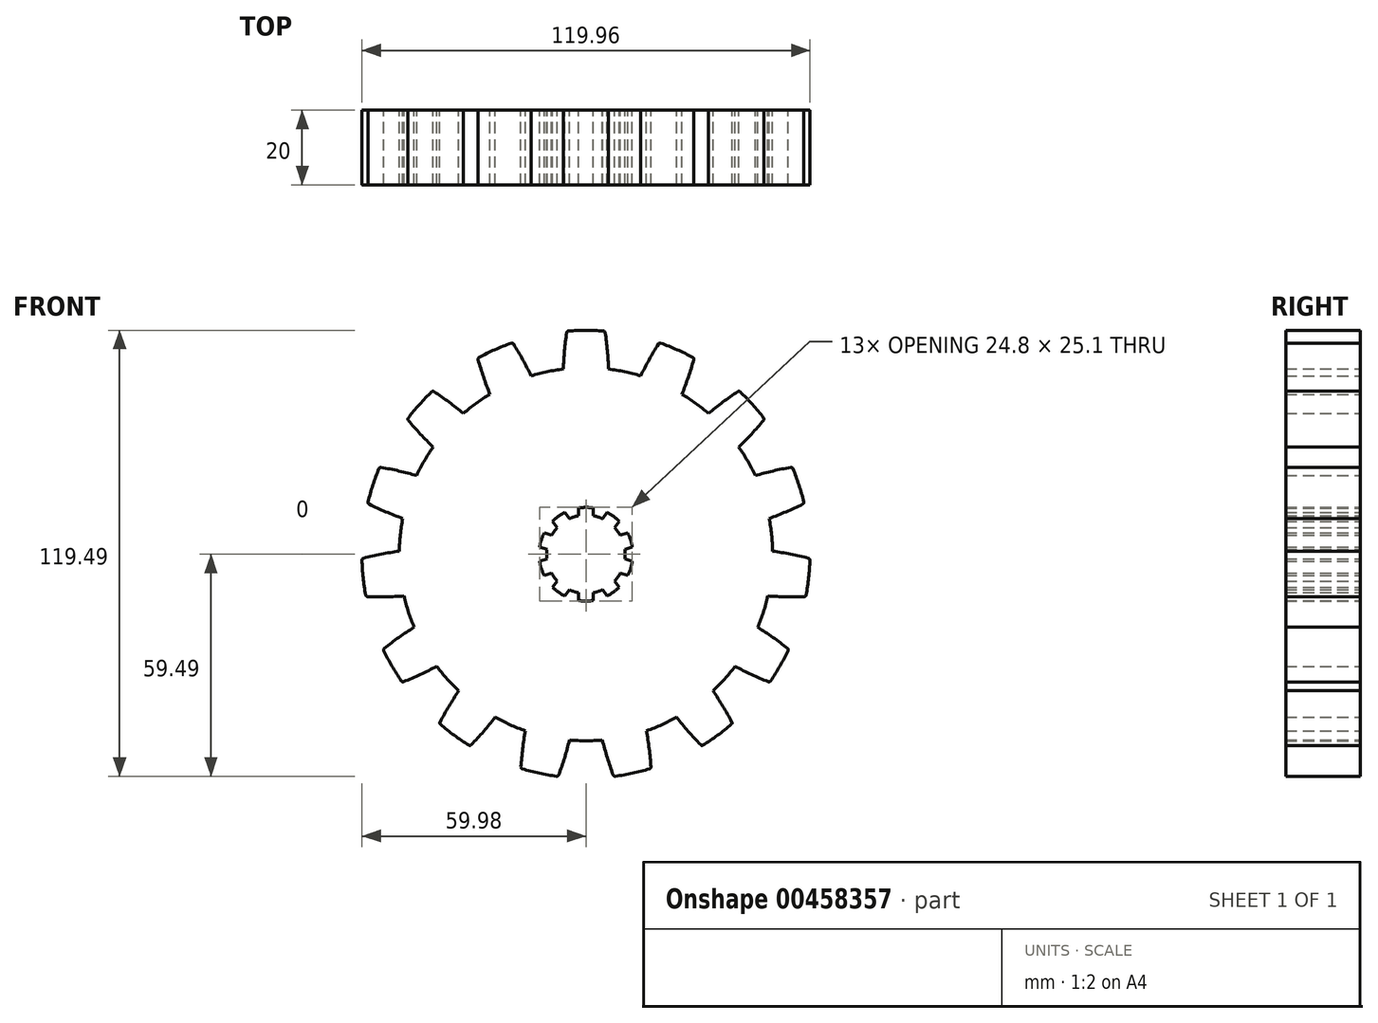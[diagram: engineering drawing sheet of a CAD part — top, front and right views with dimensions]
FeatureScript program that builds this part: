
annotation { "Feature Type Name" : "Feature", "Feature Type Description" : "" }
export const myFeature = defineFeature(function(context is Context, id is Id, definition is map)
    precondition{}
    {
        {
            var Q0;
            Q0=qCreatedBy(makeId("Front.planeOp"),FACE);
            var sketch = newSketch(context, id + "F0", { "sketchPlane" : qUnion([Q0])});
            skCircle(sketch, "E0", {"center": v(0, 0) * mm, "radius": 50 * mm});
            skArc(sketch, "E1", {"start": v(-5.11, 59.78) * mm, "mid": v(-5.72, 54.72) * mm, "end": v(-6.05, 49.63) * mm});
            skArc(sketch, "E2.trimOffspring", {"start": v(5.11, 59.78) * mm, "mid": v(0, 60) * mm, "end": v(-5.11, 59.78) * mm});
            skArc(sketch, "E3.trimOffspring", {"start": v(6.05, 49.63) * mm, "mid": v(5.72, 54.72) * mm, "end": v(5.11, 59.78) * mm});
            skPoint(sketch, "E4.start.orphan", {"position": v(0, 46.5) * mm});
            skArc(sketch, "E5.1.0", {"start": v(-19.64, 56.7) * mm, "mid": v(-24.4, 54.81) * mm, "end": v(-28.99, 52.53) * mm});
            skArc(sketch, "E5.1.1", {"start": v(-14.66, 47.8) * mm, "mid": v(-17.03, 52.32) * mm, "end": v(-19.64, 56.7) * mm});
            skArc(sketch, "E5.1.2", {"start": v(-28.99, 52.53) * mm, "mid": v(-27.49, 47.66) * mm, "end": v(-25.71, 42.88) * mm});
            skArc(sketch, "E5.2.0", {"start": v(-41, 43.8) * mm, "mid": v(-44.59, 40.15) * mm, "end": v(-47.85, 36.2) * mm});
            skArc(sketch, "E5.2.1", {"start": v(-32.84, 37.7) * mm, "mid": v(-36.84, 40.87) * mm, "end": v(-41, 43.8) * mm});
            skArc(sketch, "E5.2.2", {"start": v(-47.85, 36.2) * mm, "mid": v(-44.5, 32.36) * mm, "end": v(-40.93, 28.72) * mm});
            skArc(sketch, "E6.3.3.0", {"start": v(-55.28, 23.34) * mm, "mid": v(-57.06, 18.54) * mm, "end": v(-58.44, 13.6) * mm});
            skArc(sketch, "E6.4.3.0", {"start": v(-45.34, 21.09) * mm, "mid": v(-50.27, 22.35) * mm, "end": v(-55.28, 23.34) * mm});
            skArc(sketch, "E6.8.3.0", {"start": v(-58.44, 13.6) * mm, "mid": v(-53.81, 11.47) * mm, "end": v(-49.07, 9.59) * mm});
            skArc(sketch, "E6.3.4.0", {"start": v(-59.99, -1.16) * mm, "mid": v(-59.67, -6.27) * mm, "end": v(-58.92, -11.34) * mm});
            skArc(sketch, "E6.4.4.0", {"start": v(-50, 0.82) * mm, "mid": v(-55.02, -0.03) * mm, "end": v(-59.99, -1.16) * mm});
            skArc(sketch, "E6.8.4.0", {"start": v(-58.92, -11.34) * mm, "mid": v(-53.82, -11.41) * mm, "end": v(-48.73, -11.2) * mm});
            skArc(sketch, "E6.3.5.0", {"start": v(-54.33, -25.46) * mm, "mid": v(-51.96, -30) * mm, "end": v(-49.22, -34.32) * mm});
            skArc(sketch, "E6.4.5.0", {"start": v(-46, -19.58) * mm, "mid": v(-50.25, -22.4) * mm, "end": v(-54.33, -25.46) * mm});
            skArc(sketch, "E6.8.5.0", {"start": v(-49.22, -34.32) * mm, "mid": v(-44.53, -32.32) * mm, "end": v(-39.96, -30.05) * mm});
            skArc(sketch, "E6.3.6.0", {"start": v(-39.28, -45.36) * mm, "mid": v(-35.27, -48.54) * mm, "end": v(-31, -51.37) * mm});
            skArc(sketch, "E6.4.6.0", {"start": v(-34.06, -36.6) * mm, "mid": v(-36.8, -40.9) * mm, "end": v(-39.28, -45.36) * mm});
            skArc(sketch, "E6.8.6.0", {"start": v(-31, -51.37) * mm, "mid": v(-27.53, -47.63) * mm, "end": v(-24.28, -43.7) * mm});
            skArc(sketch, "E6.3.7.0", {"start": v(-17.43, -57.41) * mm, "mid": v(-12.47, -58.69) * mm, "end": v(-7.43, -59.54) * mm});
            skArc(sketch, "E6.4.7.0", {"start": v(-16.23, -47.3) * mm, "mid": v(-16.98, -52.33) * mm, "end": v(-17.43, -57.41) * mm});
            skArc(sketch, "E6.8.7.0", {"start": v(-7.43, -59.54) * mm, "mid": v(-5.78, -54.71) * mm, "end": v(-4.4, -49.8) * mm});
            skArc(sketch, "E6.3.8.0", {"start": v(7.43, -59.54) * mm, "mid": v(12.47, -58.69) * mm, "end": v(17.43, -57.41) * mm});
            skArc(sketch, "E6.4.8.0", {"start": v(4.4, -49.8) * mm, "mid": v(5.78, -54.71) * mm, "end": v(7.43, -59.54) * mm});
            skArc(sketch, "E6.8.8.0", {"start": v(17.43, -57.41) * mm, "mid": v(16.98, -52.33) * mm, "end": v(16.23, -47.3) * mm});
            skArc(sketch, "E6.3.9.0", {"start": v(31, -51.37) * mm, "mid": v(35.27, -48.54) * mm, "end": v(39.28, -45.36) * mm});
            skArc(sketch, "E6.4.9.0", {"start": v(24.28, -43.7) * mm, "mid": v(27.53, -47.63) * mm, "end": v(31, -51.37) * mm});
            skArc(sketch, "E6.8.9.0", {"start": v(39.28, -45.36) * mm, "mid": v(36.8, -40.9) * mm, "end": v(34.06, -36.6) * mm});
            skArc(sketch, "E7", {"start": v(-7.68, 7.16) * mm, "mid": v(-8.5, 6.17) * mm, "end": v(-9.19, 5.09) * mm});
            skArc(sketch, "E8", {"start": v(2, 12.39) * mm, "mid": v(0, 12.55) * mm, "end": v(-2, 12.39) * mm});
            skLineSegment(sketch, "E9.left", {"start": v(2, 12.39) * mm, "end": v(2, 10.3) * mm});
            skLineSegment(sketch, "E9.right", {"start": v(-2, 12.39) * mm, "end": v(-2, 10.3) * mm});
            skPoint(sketch, "E10.orphan", {"position": v(-2, 13) * mm});
            skPoint(sketch, "E11.orphan", {"position": v(2, 13) * mm});
            skPoint(sketch, "E12.trimOffspring.end.orphan", {"position": v(2, -13) * mm});
            skPoint(sketch, "E13.trimOffspring.end.orphan", {"position": v(-2, -13) * mm});
            skArc(sketch, "E14.1.0", {"start": v(-5.66, 11.2) * mm, "mid": v(-7.38, 10.15) * mm, "end": v(-8.9, 8.85) * mm});
            skLineSegment(sketch, "E14.1.1", {"start": v(-8.9, 8.85) * mm, "end": v(-7.68, 7.16) * mm});
            skLineSegment(sketch, "E14.1.2", {"start": v(-5.66, 11.2) * mm, "end": v(-4.44, 9.51) * mm});
            skArc(sketch, "E14.2.0", {"start": v(-11.17, 5.73) * mm, "mid": v(-11.94, 3.88) * mm, "end": v(-12.4, 1.93) * mm});
            skLineSegment(sketch, "E14.2.1", {"start": v(-12.4, 1.93) * mm, "end": v(-10.42, 1.28) * mm});
            skLineSegment(sketch, "E14.2.2", {"start": v(-11.17, 5.73) * mm, "end": v(-9.19, 5.09) * mm});
            skArc(sketch, "E15.3.3.0", {"start": v(-12.4, -1.93) * mm, "mid": v(-11.94, -3.88) * mm, "end": v(-11.17, -5.73) * mm});
            skLineSegment(sketch, "E15.4.3.0", {"start": v(-11.17, -5.73) * mm, "end": v(-9.19, -5.09) * mm});
            skLineSegment(sketch, "E15.7.3.0", {"start": v(-12.4, -1.93) * mm, "end": v(-10.42, -1.28) * mm});
            skArc(sketch, "E15.3.4.0", {"start": v(-8.9, -8.85) * mm, "mid": v(-7.38, -10.15) * mm, "end": v(-5.66, -11.2) * mm});
            skLineSegment(sketch, "E15.4.4.0", {"start": v(-5.66, -11.2) * mm, "end": v(-4.44, -9.51) * mm});
            skLineSegment(sketch, "E15.7.4.0", {"start": v(-8.9, -8.85) * mm, "end": v(-7.68, -7.16) * mm});
            skArc(sketch, "E15.3.5.0", {"start": v(-2, -12.39) * mm, "mid": v(0, -12.55) * mm, "end": v(2, -12.39) * mm});
            skLineSegment(sketch, "E15.4.5.0", {"start": v(2, -12.39) * mm, "end": v(2, -10.3) * mm});
            skLineSegment(sketch, "E15.7.5.0", {"start": v(-2, -12.39) * mm, "end": v(-2, -10.3) * mm});
            skArc(sketch, "E15.3.6.0", {"start": v(5.66, -11.2) * mm, "mid": v(7.38, -10.15) * mm, "end": v(8.9, -8.85) * mm});
            skLineSegment(sketch, "E15.4.6.0", {"start": v(8.9, -8.85) * mm, "end": v(7.68, -7.16) * mm});
            skLineSegment(sketch, "E15.7.6.0", {"start": v(5.66, -11.2) * mm, "end": v(4.44, -9.51) * mm});
            skArc(sketch, "E15.3.7.0", {"start": v(11.17, -5.73) * mm, "mid": v(11.94, -3.88) * mm, "end": v(12.4, -1.93) * mm});
            skLineSegment(sketch, "E15.4.7.0", {"start": v(12.4, -1.93) * mm, "end": v(10.42, -1.28) * mm});
            skLineSegment(sketch, "E15.7.7.0", {"start": v(11.17, -5.73) * mm, "end": v(9.19, -5.09) * mm});
            skArc(sketch, "E15.3.8.0", {"start": v(12.4, 1.93) * mm, "mid": v(11.94, 3.88) * mm, "end": v(11.17, 5.73) * mm});
            skLineSegment(sketch, "E15.4.8.0", {"start": v(11.17, 5.73) * mm, "end": v(9.19, 5.09) * mm});
            skLineSegment(sketch, "E15.7.8.0", {"start": v(12.4, 1.93) * mm, "end": v(10.42, 1.28) * mm});
            skArc(sketch, "E15.3.9.0", {"start": v(8.9, 8.85) * mm, "mid": v(7.38, 10.15) * mm, "end": v(5.66, 11.2) * mm});
            skLineSegment(sketch, "E15.4.9.0", {"start": v(5.66, 11.2) * mm, "end": v(4.44, 9.51) * mm});
            skLineSegment(sketch, "E15.7.9.0", {"start": v(8.9, 8.85) * mm, "end": v(7.68, 7.16) * mm});
            skArc(sketch, "E16.trimOffspring", {"start": v(-2, 10.3) * mm, "mid": v(-3.24, 9.99) * mm, "end": v(-4.44, 9.51) * mm});
            skArc(sketch, "E17.trimOffspring", {"start": v(4.44, 9.51) * mm, "mid": v(3.24, 9.99) * mm, "end": v(2, 10.3) * mm});
            skArc(sketch, "E18.trimOffspring", {"start": v(9.19, 5.09) * mm, "mid": v(8.5, 6.17) * mm, "end": v(7.68, 7.16) * mm});
            skArc(sketch, "E19.trimOffspring", {"start": v(10.42, -1.28) * mm, "mid": v(10.5, 0) * mm, "end": v(10.42, 1.28) * mm});
            skArc(sketch, "E20.trimOffspring", {"start": v(7.68, -7.16) * mm, "mid": v(8.5, -6.17) * mm, "end": v(9.19, -5.09) * mm});
            skArc(sketch, "E21.trimOffspring", {"start": v(2, -10.3) * mm, "mid": v(3.24, -9.99) * mm, "end": v(4.44, -9.51) * mm});
            skArc(sketch, "E22.trimOffspring", {"start": v(-4.44, -9.51) * mm, "mid": v(-3.24, -9.99) * mm, "end": v(-2, -10.3) * mm});
            skArc(sketch, "E23.trimOffspring", {"start": v(-9.19, -5.09) * mm, "mid": v(-8.5, -6.17) * mm, "end": v(-7.68, -7.16) * mm});
            skArc(sketch, "E24.trimOffspring", {"start": v(-10.42, 1.28) * mm, "mid": v(-10.5, 0) * mm, "end": v(-10.42, -1.28) * mm});
            skArc(sketch, "E25.3.10.0", {"start": v(49.22, -34.32) * mm, "mid": v(51.96, -30) * mm, "end": v(54.33, -25.46) * mm});
            skArc(sketch, "E25.4.10.0", {"start": v(39.96, -30.05) * mm, "mid": v(44.53, -32.32) * mm, "end": v(49.22, -34.32) * mm});
            skArc(sketch, "E25.8.10.0", {"start": v(54.33, -25.46) * mm, "mid": v(50.25, -22.4) * mm, "end": v(46, -19.58) * mm});
            skArc(sketch, "E25.3.11.0", {"start": v(58.92, -11.34) * mm, "mid": v(59.67, -6.27) * mm, "end": v(59.99, -1.16) * mm});
            skArc(sketch, "E25.4.11.0", {"start": v(48.73, -11.2) * mm, "mid": v(53.82, -11.41) * mm, "end": v(58.92, -11.34) * mm});
            skArc(sketch, "E25.8.11.0", {"start": v(59.99, -1.16) * mm, "mid": v(55.02, -0.03) * mm, "end": v(50, 0.82) * mm});
            skArc(sketch, "E25.3.12.0", {"start": v(58.44, 13.6) * mm, "mid": v(57.06, 18.54) * mm, "end": v(55.28, 23.34) * mm});
            skArc(sketch, "E25.4.12.0", {"start": v(49.07, 9.59) * mm, "mid": v(53.81, 11.47) * mm, "end": v(58.44, 13.6) * mm});
            skArc(sketch, "E25.8.12.0", {"start": v(55.28, 23.34) * mm, "mid": v(50.27, 22.35) * mm, "end": v(45.34, 21.09) * mm});
            skArc(sketch, "E25.3.13.0", {"start": v(47.85, 36.2) * mm, "mid": v(44.59, 40.15) * mm, "end": v(41, 43.8) * mm});
            skArc(sketch, "E25.4.13.0", {"start": v(40.93, 28.72) * mm, "mid": v(44.5, 32.36) * mm, "end": v(47.85, 36.2) * mm});
            skArc(sketch, "E25.8.13.0", {"start": v(41, 43.8) * mm, "mid": v(36.84, 40.87) * mm, "end": v(32.84, 37.7) * mm});
            skArc(sketch, "E25.3.14.0", {"start": v(28.99, 52.53) * mm, "mid": v(24.4, 54.81) * mm, "end": v(19.64, 56.7) * mm});
            skArc(sketch, "E25.4.14.0", {"start": v(25.71, 42.88) * mm, "mid": v(27.49, 47.66) * mm, "end": v(28.99, 52.53) * mm});
            skArc(sketch, "E25.8.14.0", {"start": v(19.64, 56.7) * mm, "mid": v(17.03, 52.32) * mm, "end": v(14.66, 47.8) * mm});
            skSolve(sketch);
        }
        {
            var Q0;
            Q0=makeQuery(id+"F0.imprint","IMPRINT",FACE,{"disambiguationData":[TD([[makeQuery(id+"F0.imprint","IMPRINT",EDGE,{"derivedFrom":sQuery(id+"F0.wireOp",EDGE,"E6.3.5.0")}),1.0]])]});
            var Q1;
            Q1=makeQuery(id+"F0.imprint","IMPRINT",FACE,{"disambiguationData":[TD([[makeQuery(id+"F0.imprint","IMPRINT",EDGE,{"derivedFrom":sQuery(id+"F0.wireOp",EDGE,"E6.3.7.0")}),1.0]])]});
            var Q2;
            Q2=makeQuery(id+"F0.imprint","IMPRINT",FACE,{"disambiguationData":[TD([[makeQuery(id+"F0.imprint","IMPRINT",EDGE,{"derivedFrom":sQuery(id+"F0.wireOp",EDGE,"E5.2.0")}),1.0]])]});
            var Q3;
            Q3=makeQuery(id+"F0.imprint","IMPRINT",FACE,{"disambiguationData":[TD([[makeQuery(id+"F0.imprint","IMPRINT",EDGE,{"derivedFrom":sQuery(id+"F0.wireOp",EDGE,"E6.3.3.0")}),1.0]])]});
            var Q4;
            Q4=makeQuery(id+"F0.imprint","IMPRINT",FACE,{"disambiguationData":[TD([[makeQuery(id+"F0.imprint","IMPRINT",EDGE,{"derivedFrom":sQuery(id+"F0.wireOp",EDGE,"E6.3.4.0")}),1.0]])]});
            var Q5;
            Q5=makeQuery(id+"F0.imprint","IMPRINT",FACE,{"disambiguationData":[TD([[makeQuery(id+"F0.imprint","IMPRINT",EDGE,{"derivedFrom":sQuery(id+"F0.wireOp",EDGE,"E6.3.6.0")}),1.0]])]});
            var Q6;
            Q6=makeQuery(id+"F0.imprint","IMPRINT",FACE,{"disambiguationData":[TD([[makeQuery(id+"F0.imprint","IMPRINT",EDGE,{"derivedFrom":sQuery(id+"F0.wireOp",EDGE,"E7")}),-1.0]])]});
            var Q7;
            Q7=makeQuery(id+"F0.imprint","IMPRINT",FACE,{"disambiguationData":[TD([[makeQuery(id+"F0.imprint","IMPRINT",EDGE,{"derivedFrom":sQuery(id+"F0.wireOp",EDGE,"E6.3.9.0")}),1.0]])]});
            var Q8;
            Q8=makeQuery(id+"F0.imprint","IMPRINT",FACE,{"disambiguationData":[TD([[makeQuery(id+"F0.imprint","IMPRINT",EDGE,{"derivedFrom":sQuery(id+"F0.wireOp",EDGE,"E5.1.0")}),1.0]])]});
            var Q9;
            Q9=makeQuery(id+"F0.imprint","IMPRINT",FACE,{"disambiguationData":[TD([[makeQuery(id+"F0.imprint","IMPRINT",EDGE,{"derivedFrom":sQuery(id+"F0.wireOp",EDGE,"E6.3.8.0")}),1.0]])]});
            var Q10;
            {var subQ0=sQuery(id+"F0.wireOp",EDGE,"E1");Q10=makeQuery(id+"F0.imprint","IMPRINT",FACE,{"disambiguationData":[TD([[makeQuery(id+"F0.imprint","IMPRINT",EDGE,{"derivedFrom":subQ0}),1.0]])]});}
            var Q11;
            Q11=makeQuery(id+"F0.imprint","IMPRINT",FACE,{"disambiguationData":[TD([[makeQuery(id+"F0.imprint","IMPRINT",EDGE,{"derivedFrom":sQuery(id+"F0.wireOp",EDGE,"E25.3.14.0")}),1.0]])]});
            var Q12;
            Q12=makeQuery(id+"F0.imprint","IMPRINT",FACE,{"disambiguationData":[TD([[makeQuery(id+"F0.imprint","IMPRINT",EDGE,{"derivedFrom":sQuery(id+"F0.wireOp",EDGE,"E25.3.13.0")}),1.0]])]});
            var Q13;
            Q13=makeQuery(id+"F0.imprint","IMPRINT",FACE,{"disambiguationData":[TD([[makeQuery(id+"F0.imprint","IMPRINT",EDGE,{"derivedFrom":sQuery(id+"F0.wireOp",EDGE,"E25.3.12.0")}),1.0]])]});
            var Q14;
            Q14=makeQuery(id+"F0.imprint","IMPRINT",FACE,{"disambiguationData":[TD([[makeQuery(id+"F0.imprint","IMPRINT",EDGE,{"derivedFrom":sQuery(id+"F0.wireOp",EDGE,"E25.3.11.0")}),1.0]])]});
            var Q15;
            Q15=makeQuery(id+"F0.imprint","IMPRINT",FACE,{"disambiguationData":[TD([[makeQuery(id+"F0.imprint","IMPRINT",EDGE,{"derivedFrom":sQuery(id+"F0.wireOp",EDGE,"E25.3.10.0")}),1.0]])]});
            extrude(context, id + "F1", {"entities" : qUnion([Q0, Q1, Q2, Q3, Q4, Q5, Q6, Q7, Q8, Q9, Q10, Q11, Q12, Q13, Q14, Q15]), "depth" : 20 * mm});
        }
        {
            var Q0;
            Q0=makeQuery(id+"F1.opExtrude","SWEPT_EDGE",EDGE,{"disambiguationData":[OSD([sQuery(id+"F0.wireOp",EDGE,"E1"),sQuery(id+"F0.wireOp",EDGE,"E2.trimOffspring")])]});
            var Q1;
            Q1=makeQuery(id+"F1.opExtrude","SWEPT_EDGE",EDGE,{"disambiguationData":[OSD([sQuery(id+"F0.wireOp",EDGE,"E2.trimOffspring"),sQuery(id+"F0.wireOp",EDGE,"E3.trimOffspring")])]});
            var Q2;
            Q2=makeQuery(id+"F1.opExtrude","SWEPT_EDGE",EDGE,{"disambiguationData":[OSD([sQuery(id+"F0.wireOp",EDGE,"E25.3.14.0"),sQuery(id+"F0.wireOp",EDGE,"E25.8.14.0")])]});
            var Q3;
            Q3=makeQuery(id+"F1.opExtrude","SWEPT_EDGE",EDGE,{"disambiguationData":[OSD([sQuery(id+"F0.wireOp",EDGE,"E25.3.14.0"),sQuery(id+"F0.wireOp",EDGE,"E25.4.14.0")])]});
            var Q4;
            Q4=makeQuery(id+"F1.opExtrude","SWEPT_EDGE",EDGE,{"disambiguationData":[OSD([sQuery(id+"F0.wireOp",EDGE,"E25.3.13.0"),sQuery(id+"F0.wireOp",EDGE,"E25.8.13.0")])]});
            var Q5;
            Q5=makeQuery(id+"F1.opExtrude","SWEPT_EDGE",EDGE,{"disambiguationData":[OSD([sQuery(id+"F0.wireOp",EDGE,"E25.3.13.0"),sQuery(id+"F0.wireOp",EDGE,"E25.4.13.0")])]});
            var Q6;
            Q6=makeQuery(id+"F1.opExtrude","SWEPT_EDGE",EDGE,{"disambiguationData":[OSD([sQuery(id+"F0.wireOp",EDGE,"E25.3.12.0"),sQuery(id+"F0.wireOp",EDGE,"E25.8.12.0")])]});
            var Q7;
            Q7=makeQuery(id+"F1.opExtrude","SWEPT_EDGE",EDGE,{"disambiguationData":[OSD([sQuery(id+"F0.wireOp",EDGE,"E25.3.12.0"),sQuery(id+"F0.wireOp",EDGE,"E25.4.12.0")])]});
            var Q8;
            Q8=makeQuery(id+"F1.opExtrude","SWEPT_EDGE",EDGE,{"disambiguationData":[OSD([sQuery(id+"F0.wireOp",EDGE,"E25.3.11.0"),sQuery(id+"F0.wireOp",EDGE,"E25.8.11.0")])]});
            var Q9;
            Q9=makeQuery(id+"F1.opExtrude","SWEPT_EDGE",EDGE,{"disambiguationData":[OSD([sQuery(id+"F0.wireOp",EDGE,"E25.3.11.0"),sQuery(id+"F0.wireOp",EDGE,"E25.4.11.0")])]});
            var Q10;
            Q10=makeQuery(id+"F1.opExtrude","SWEPT_EDGE",EDGE,{"disambiguationData":[OSD([sQuery(id+"F0.wireOp",EDGE,"E25.3.10.0"),sQuery(id+"F0.wireOp",EDGE,"E25.8.10.0")])]});
            var Q11;
            Q11=makeQuery(id+"F1.opExtrude","SWEPT_EDGE",EDGE,{"disambiguationData":[OSD([sQuery(id+"F0.wireOp",EDGE,"E25.3.10.0"),sQuery(id+"F0.wireOp",EDGE,"E25.4.10.0")])]});
            var Q12;
            Q12=makeQuery(id+"F1.opExtrude","SWEPT_EDGE",EDGE,{"disambiguationData":[OSD([sQuery(id+"F0.wireOp",EDGE,"E6.3.9.0"),sQuery(id+"F0.wireOp",EDGE,"E6.8.9.0")])]});
            var Q13;
            Q13=makeQuery(id+"F1.opExtrude","SWEPT_EDGE",EDGE,{"disambiguationData":[OSD([sQuery(id+"F0.wireOp",EDGE,"E6.3.9.0"),sQuery(id+"F0.wireOp",EDGE,"E6.4.9.0")])]});
            var Q14;
            Q14=makeQuery(id+"F1.opExtrude","SWEPT_EDGE",EDGE,{"disambiguationData":[OSD([sQuery(id+"F0.wireOp",EDGE,"E6.3.8.0"),sQuery(id+"F0.wireOp",EDGE,"E6.8.8.0")])]});
            var Q15;
            Q15=makeQuery(id+"F1.opExtrude","SWEPT_EDGE",EDGE,{"disambiguationData":[OSD([sQuery(id+"F0.wireOp",EDGE,"E6.3.8.0"),sQuery(id+"F0.wireOp",EDGE,"E6.4.8.0")])]});
            var Q16;
            Q16=makeQuery(id+"F1.opExtrude","SWEPT_EDGE",EDGE,{"disambiguationData":[OSD([sQuery(id+"F0.wireOp",EDGE,"E6.3.7.0"),sQuery(id+"F0.wireOp",EDGE,"E6.8.7.0")])]});
            var Q17;
            Q17=makeQuery(id+"F1.opExtrude","SWEPT_EDGE",EDGE,{"disambiguationData":[OSD([sQuery(id+"F0.wireOp",EDGE,"E6.3.7.0"),sQuery(id+"F0.wireOp",EDGE,"E6.4.7.0")])]});
            var Q18;
            Q18=makeQuery(id+"F1.opExtrude","SWEPT_EDGE",EDGE,{"disambiguationData":[OSD([sQuery(id+"F0.wireOp",EDGE,"E6.3.6.0"),sQuery(id+"F0.wireOp",EDGE,"E6.8.6.0")])]});
            var Q19;
            Q19=makeQuery(id+"F1.opExtrude","SWEPT_EDGE",EDGE,{"disambiguationData":[OSD([sQuery(id+"F0.wireOp",EDGE,"E6.3.6.0"),sQuery(id+"F0.wireOp",EDGE,"E6.4.6.0")])]});
            var Q20;
            Q20=makeQuery(id+"F1.opExtrude","SWEPT_EDGE",EDGE,{"disambiguationData":[OSD([sQuery(id+"F0.wireOp",EDGE,"E6.3.5.0"),sQuery(id+"F0.wireOp",EDGE,"E6.8.5.0")])]});
            var Q21;
            Q21=makeQuery(id+"F1.opExtrude","SWEPT_EDGE",EDGE,{"disambiguationData":[OSD([sQuery(id+"F0.wireOp",EDGE,"E6.3.4.0"),sQuery(id+"F0.wireOp",EDGE,"E6.8.4.0")])]});
            var Q22;
            Q22=makeQuery(id+"F1.opExtrude","SWEPT_EDGE",EDGE,{"disambiguationData":[OSD([sQuery(id+"F0.wireOp",EDGE,"E6.3.5.0"),sQuery(id+"F0.wireOp",EDGE,"E6.4.5.0")])]});
            var Q23;
            Q23=makeQuery(id+"F1.opExtrude","SWEPT_EDGE",EDGE,{"disambiguationData":[OSD([sQuery(id+"F0.wireOp",EDGE,"E6.3.4.0"),sQuery(id+"F0.wireOp",EDGE,"E6.4.4.0")])]});
            var Q24;
            Q24=makeQuery(id+"F1.opExtrude","SWEPT_EDGE",EDGE,{"disambiguationData":[OSD([sQuery(id+"F0.wireOp",EDGE,"E6.3.3.0"),sQuery(id+"F0.wireOp",EDGE,"E6.8.3.0")])]});
            var Q25;
            Q25=makeQuery(id+"F1.opExtrude","SWEPT_EDGE",EDGE,{"disambiguationData":[OSD([sQuery(id+"F0.wireOp",EDGE,"E6.3.3.0"),sQuery(id+"F0.wireOp",EDGE,"E6.4.3.0")])]});
            var Q26;
            Q26=makeQuery(id+"F1.opExtrude","SWEPT_EDGE",EDGE,{"disambiguationData":[OSD([sQuery(id+"F0.wireOp",EDGE,"E5.2.0"),sQuery(id+"F0.wireOp",EDGE,"E5.2.2")])]});
            var Q27;
            Q27=makeQuery(id+"F1.opExtrude","SWEPT_EDGE",EDGE,{"disambiguationData":[OSD([sQuery(id+"F0.wireOp",EDGE,"E5.2.0"),sQuery(id+"F0.wireOp",EDGE,"E5.2.1")])]});
            var Q28;
            Q28=makeQuery(id+"F1.opExtrude","SWEPT_EDGE",EDGE,{"disambiguationData":[OSD([sQuery(id+"F0.wireOp",EDGE,"E5.1.0"),sQuery(id+"F0.wireOp",EDGE,"E5.1.2")])]});
            var Q29;
            Q29=makeQuery(id+"F1.opExtrude","SWEPT_EDGE",EDGE,{"disambiguationData":[OSD([sQuery(id+"F0.wireOp",EDGE,"E5.1.0"),sQuery(id+"F0.wireOp",EDGE,"E5.1.1")])]});
            fillet(context, id + "F2", {"entities" : qUnion([Q0, Q1, Q2, Q3, Q4, Q5, Q6, Q7, Q8, Q9, Q10, Q11, Q12, Q13, Q14, Q15, Q16, Q17, Q18, Q19, Q20, Q21, Q22, Q23, Q24, Q25, Q26, Q27, Q28, Q29]), "radius" : 0.5 * mm, "tangentPropagation" : true, "allowEdgeOverflow" : false});
        }
    });
